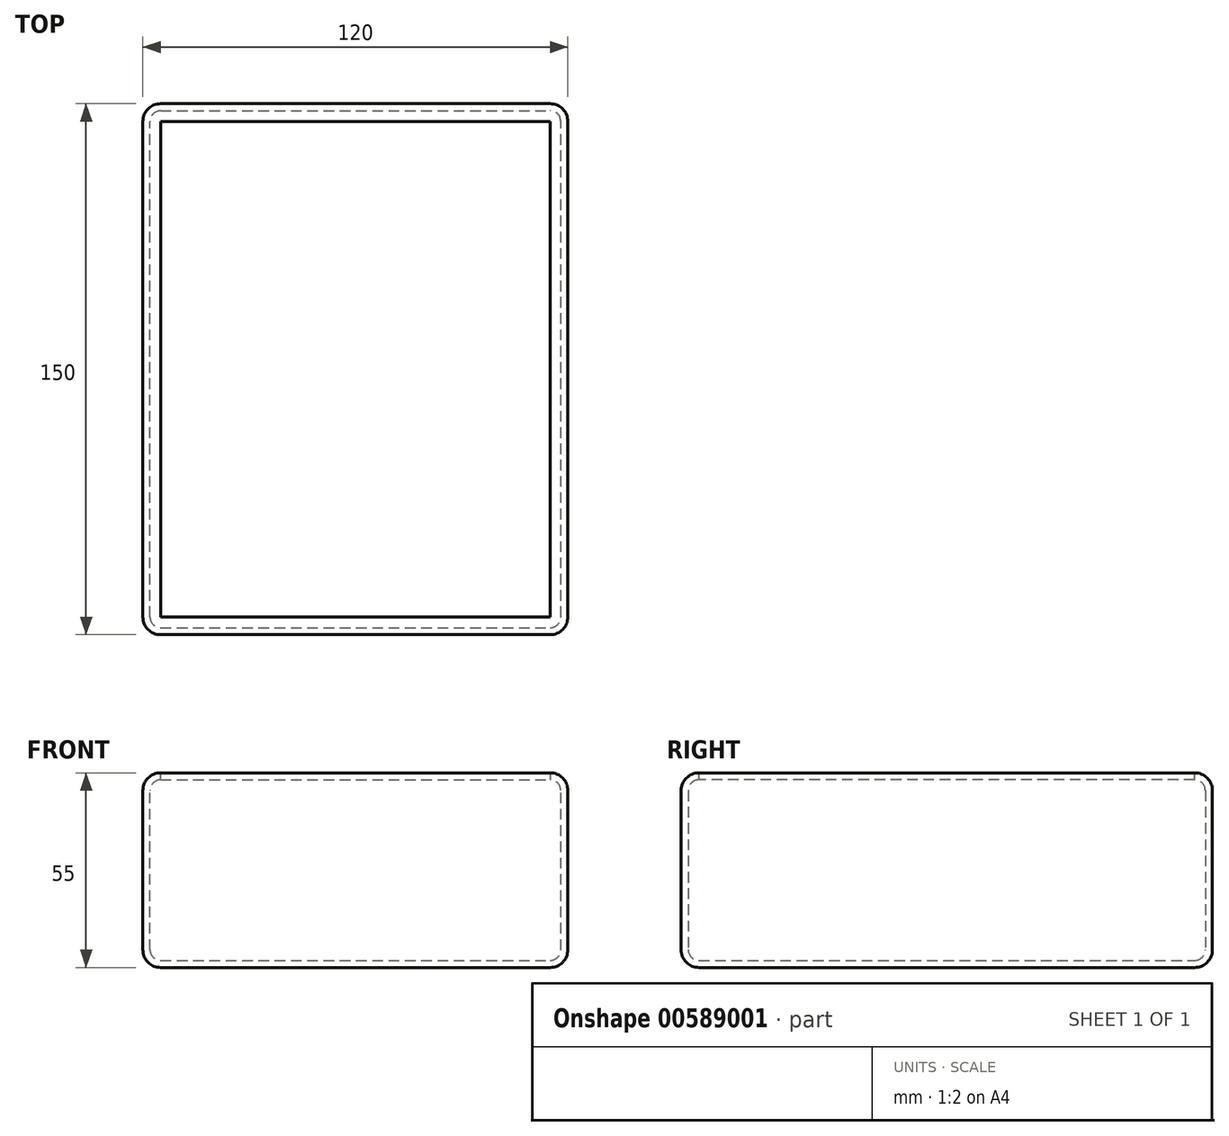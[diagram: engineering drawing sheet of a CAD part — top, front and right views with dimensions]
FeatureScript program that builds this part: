
annotation { "Feature Type Name" : "Feature", "Feature Type Description" : "" }
export const myFeature = defineFeature(function(context is Context, id is Id, definition is map)
    precondition{}
    {
        {
            var Q0;
            Q0=qCreatedBy(makeId("Top.planeOp"),FACE);
            var sketch = newSketch(context, id + "F0", { "sketchPlane" : qUnion([Q0])});
            skLineSegment(sketch, "E0.bottom", {"start": v(55, -75) * mm, "end": v(-55, -75) * mm});
            skLineSegment(sketch, "E0.top", {"start": v(55, 75) * mm, "end": v(-55, 75) * mm});
            skLineSegment(sketch, "E0.left", {"start": v(60, -70) * mm, "end": v(60, 70) * mm});
            skLineSegment(sketch, "E0.right", {"start": v(-60, -70) * mm, "end": v(-60, 70) * mm});
            skPoint(sketch, "E0.middle", {"position": v(0, 0) * mm});
            skPoint(sketch, "E1.visualSharp", {"position": v(-60, 75) * mm});
            skArc(sketch, "E1.filletArc", {"start": v(-55, 75) * mm, "mid": v(-58.54, 73.54) * mm, "end": v(-60, 70) * mm});
            skPoint(sketch, "E2.visualSharp", {"position": v(60, 75) * mm});
            skArc(sketch, "E2.filletArc", {"start": v(60, 70) * mm, "mid": v(58.54, 73.54) * mm, "end": v(55, 75) * mm});
            skPoint(sketch, "E3.visualSharp", {"position": v(60, -75) * mm});
            skArc(sketch, "E3.filletArc", {"start": v(55, -75) * mm, "mid": v(58.54, -73.54) * mm, "end": v(60, -70) * mm});
            skPoint(sketch, "E4.visualSharp", {"position": v(-60, -75) * mm});
            skArc(sketch, "E4.filletArc", {"start": v(-60, -70) * mm, "mid": v(-58.54, -73.54) * mm, "end": v(-55, -75) * mm});
            skSolve(sketch);
        }
        {
            var Q0;
            Q0 = qSketchRegion(id + "F0", true);
            extrude(context, id + "F1", {"entities" : qUnion([Q0]), "depth" : 55 * mm, "offsetDistance" : 25 * mm});
        }
        {
            var Q0;
            Q0=makeQuery(id+"F1.opExtrude","CAP_EDGE",EDGE,{"disambiguationData":[OSD([sQuery(id+"F0.wireOp",EDGE,"E0.right")])],"isStart":false});
            var Q1;
            Q1=makeQuery(id+"F1.opExtrude","CAP_EDGE",EDGE,{"disambiguationData":[OSD([sQuery(id+"F0.wireOp",EDGE,"E0.right")])],"isStart":true});
            fillet(context, id + "F2", {"entities" : qUnion([Q0, Q1]), "radius" : 5 * mm, "tangentPropagation" : true, "allowEdgeOverflow" : false});
        }
        {
            var Q0;
            Q0=makeQuery(id+"F1.opExtrude","CAP_FACE",FACE,{"disambiguationData":[OSD([sQuery(id+"F0.wireOp",EDGE,"E0.bottom"),sQuery(id+"F0.wireOp",EDGE,"E0.top"),sQuery(id+"F0.wireOp",EDGE,"E0.left"),sQuery(id+"F0.wireOp",EDGE,"E0.right"),sQuery(id+"F0.wireOp",EDGE,"E1.filletArc"),sQuery(id+"F0.wireOp",EDGE,"E2.filletArc"),sQuery(id+"F0.wireOp",EDGE,"E3.filletArc"),sQuery(id+"F0.wireOp",EDGE,"E4.filletArc")])],"isStart":false});
            shell(context, id + "F3", {"entities" : qUnion([Q0]), "thickness" : 2 * mm});
        }
    });
